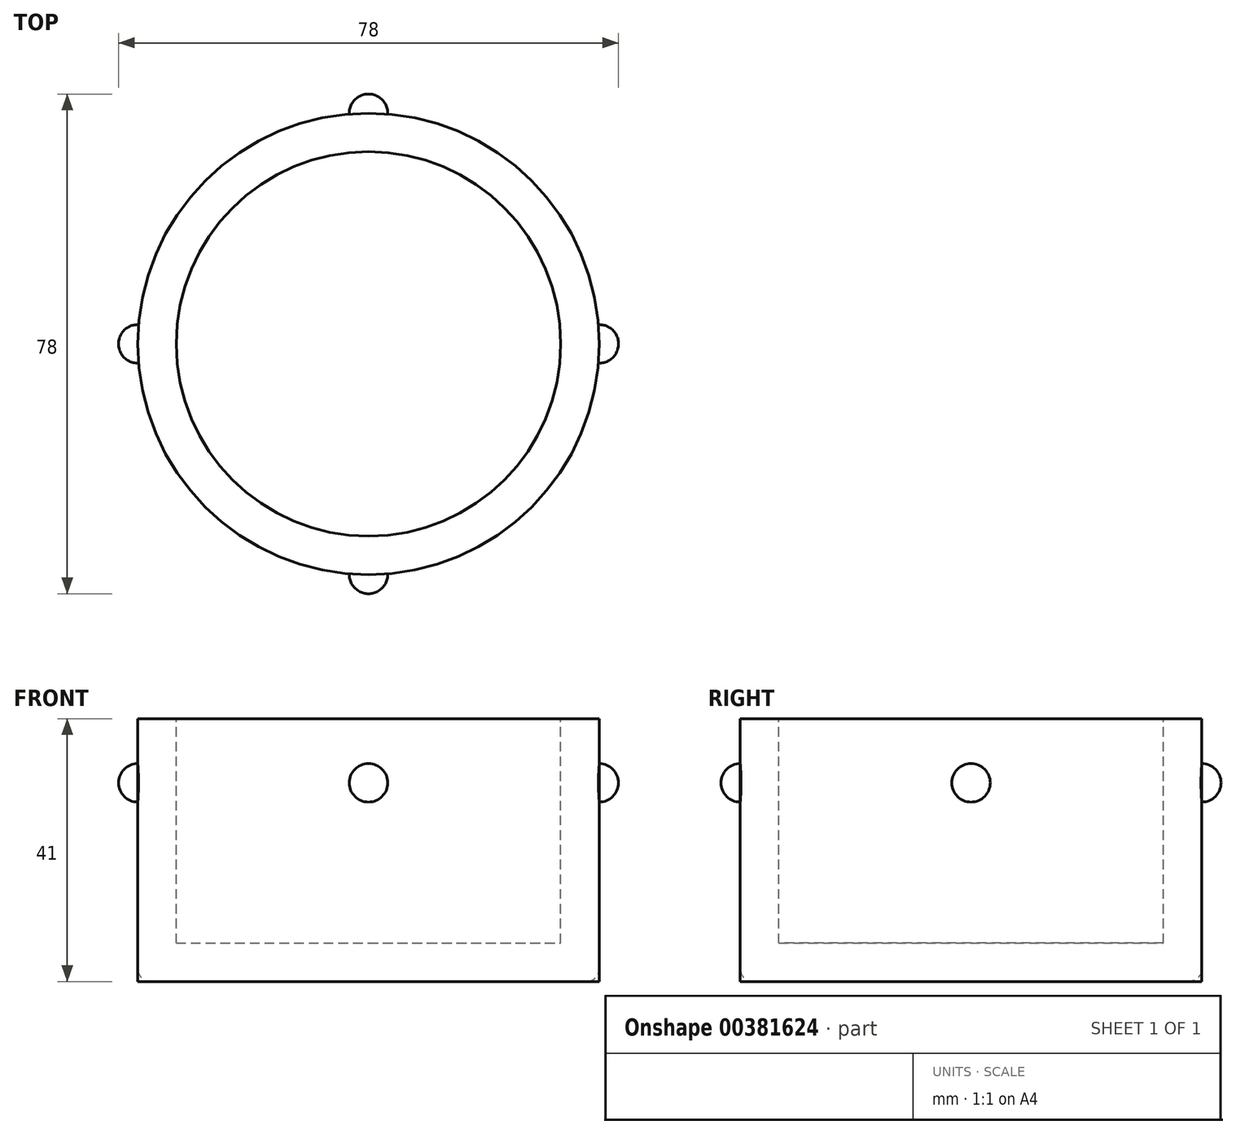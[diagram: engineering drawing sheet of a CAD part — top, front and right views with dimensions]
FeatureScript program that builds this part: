
annotation { "Feature Type Name" : "Feature", "Feature Type Description" : "" }
export const myFeature = defineFeature(function(context is Context, id is Id, definition is map)
    precondition{}
    {
        {
            var Q0;
            Q0=qCreatedBy(makeId("Top.planeOp"),FACE);
            var sketch = newSketch(context, id + "F0", { "sketchPlane" : qUnion([Q0])});
            skCircle(sketch, "E0", {"center": v(0, 0) * mm, "radius": 36 * mm});
            skSolve(sketch);
        }
        {
            var Q0;
            Q0 = qSketchRegion(id + "F0", true);
            extrude(context, id + "F1", {"entities" : qUnion([Q0]), "depth" : 41 * mm});
        }
        {
            var Q0;
            Q0=makeQuery(id+"F1.opExtrude","CAP_FACE",FACE,{"disambiguationData":[OSD([sQuery(id+"F0.wireOp",EDGE,"E0")])],"isStart":false});
            var sketch = newSketch(context, id + "F2", { "sketchPlane" : qUnion([Q0])});
            skCircle(sketch, "E1", {"center": v(0, 0) * mm, "radius": 30 * mm});
            skSolve(sketch);
        }
        {
            var Q0;
            Q0 = qSketchRegion(id + "F2", true);
            extrude(context, id + "F3", {"entities" : qUnion([Q0]), "operationType" : NewBodyOperationType.REMOVE, "oppositeDirection" : true, "depth" : 35 * mm});
        }
        {
            var Q0;
            Q0=qCreatedBy(makeId("Right.planeOp"),FACE);
            cPlane(context, id + "F4", {"entities" : qUnion([Q0]), "cplaneType" : CPlaneType.OFFSET, "offset" : 36 * mm, "width" : 152.4 * mm, "height" : 152.4 * mm});
        }
        {
            var Q0;
            Q0=qCreatedBy(id+"F4.planeOp",FACE);
            var sketch = newSketch(context, id + "F5", { "sketchPlane" : qUnion([Q0])});
            skLineSegment(sketch, "E2", {"start": v(0, 0) * mm, "end": v(0, 31) * mm});
            skArc(sketch, "E3", {"start": v(0, 28) * mm, "mid": v(3, 31) * mm, "end": v(0, 34) * mm});
            skLineSegment(sketch, "E4", {"start": v(0, 40.4) * mm, "end": v(0, 18.86) * mm});
            skSolve(sketch);
        }
        {
            var Q0;
            {var subQ0=sQuery(id+"F5.wireOp",EDGE,"E3");Q0=makeQuery(id+"F5.imprint","IMPRINT",FACE,{"disambiguationData":[TD([[makeQuery(id+"F5.imprint","IMPRINT",EDGE,{"derivedFrom":subQ0}),1.0]])]});}
            var Q1;
            Q1=sQuery(id+"F5.wireOp",EDGE,"E4");
            revolve(context, id + "F6", {"operationType" : NewBodyOperationType.ADD, "entities" : qUnion([Q0]), "axis" : qUnion([Q1]), "revolveType" : RevolveType.FULL});
        }
        {
            var Q0;
            Q0=makeQuery(id+"F1.opExtrude","SWEPT_BODY",BODY,{"disambiguationData":[OSD([sQuery(id+"F0.wireOp",EDGE,"E0")])]});
            var Q1;
            Q1=makeQuery(id+"F3.boolean.opBoolean","COPY",FACE,{"derivedFrom":makeQuery(id+"F3.opExtrude","SWEPT_FACE",FACE,{"disambiguationData":[OSD([sQuery(id+"F2.wireOp",EDGE,"E1")])]})});
            circularPattern(context, id + "F7", {"entities" : qUnion([Q0]), "axis" : qUnion([Q1]), "angle" : 360 * degree, "instanceCount" : 4, "oppositeDirection" : true, "equalSpace" : true});
        }
        {
            var Q0;
            Q0=makeQuery(id+"F1.opExtrude","CAP_EDGE",EDGE,{"disambiguationData":[OSD([sQuery(id+"F0.wireOp",EDGE,"E0")])],"isStart":true});
            fillet(context, id + "F8", {"entities" : qUnion([Q0]), "radius" : 2 * mm, "tangentPropagation" : true, "allowEdgeOverflow" : false});
        }
    });
